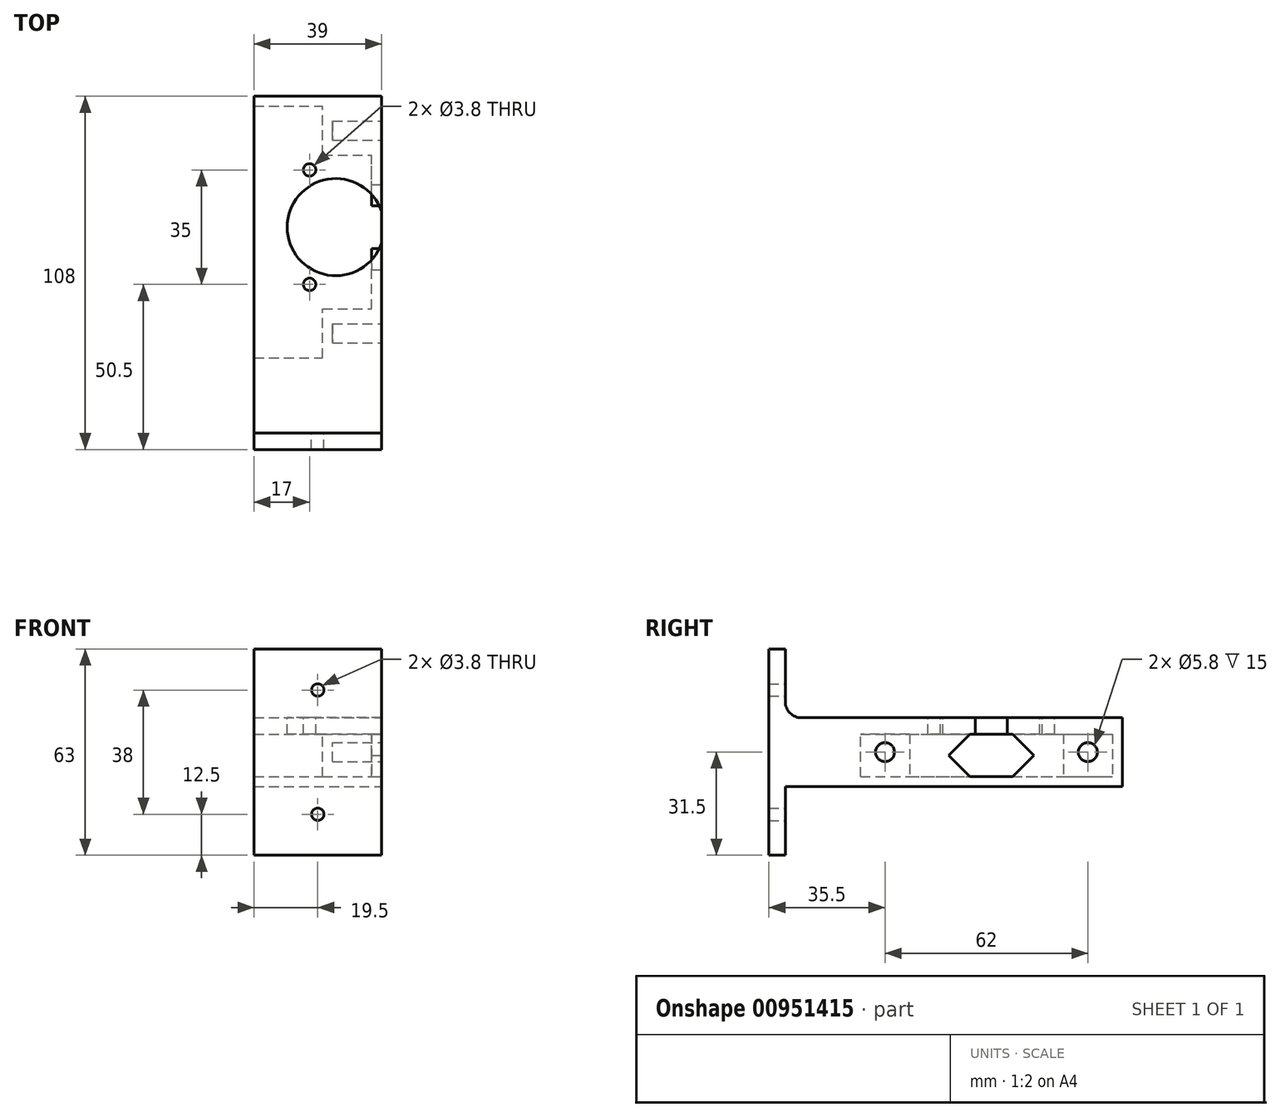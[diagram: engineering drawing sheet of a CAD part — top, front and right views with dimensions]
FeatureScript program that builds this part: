
annotation { "Feature Type Name" : "Feature", "Feature Type Description" : "" }
export const myFeature = defineFeature(function(context is Context, id is Id, definition is map)
    precondition{}
    {
        {
            var Q0;
            Q0=qCreatedBy(makeId("Top.planeOp"),FACE);
            var sketch = newSketch(context, id + "F0", { "sketchPlane" : qUnion([Q0])});
            skLineSegment(sketch, "E0", {"start": v(0, 83) * mm, "end": v(0, 0) * mm});
            skLineSegment(sketch, "E1", {"start": v(0, 0) * mm, "end": v(-39, 0) * mm});
            skLineSegment(sketch, "E2", {"start": v(-39, 0) * mm, "end": v(-39, 3) * mm});
            skLineSegment(sketch, "E3", {"start": v(-39, 3) * mm, "end": v(-3, 3) * mm});
            skLineSegment(sketch, "E4", {"start": v(-3, 3) * mm, "end": v(-3, 83) * mm});
            skLineSegment(sketch, "E5", {"start": v(-3, 83) * mm, "end": v(0, 83) * mm});
            skSolve(sketch);
        }
        {
            var Q0;
            Q0 = qSketchRegion(id + "F0", true);
            extrude(context, id + "F1", {"entities" : qUnion([Q0]), "endBound" : BoundingType.SYMMETRIC, "depth" : 18 * mm, "offsetDistance" : 25 * mm});
        }
        {
            var Q0;
            Q0=makeQuery(id+"F1.opExtrude","CAP_FACE",FACE,{"disambiguationData":[OSD([sQuery(id+"F0.wireOp",EDGE,"E0"),sQuery(id+"F0.wireOp",EDGE,"E1"),sQuery(id+"F0.wireOp",EDGE,"E2"),sQuery(id+"F0.wireOp",EDGE,"E3"),sQuery(id+"F0.wireOp",EDGE,"E4"),sQuery(id+"F0.wireOp",EDGE,"E5")])],"isStart":false});
            var sketch = newSketch(context, id + "F2", { "sketchPlane" : qUnion([Q0])});
            skLineSegment(sketch, "E6.0", {"start": v(0, 83) * mm, "end": v(0, 0) * mm});
            skLineSegment(sketch, "E6.1", {"start": v(0, 0) * mm, "end": v(-39, 0) * mm});
            skLineSegment(sketch, "E7", {"start": v(-39, 0) * mm, "end": v(-39, 83) * mm});
            skLineSegment(sketch, "E8", {"start": v(-39, 83) * mm, "end": v(0, 83) * mm});
            skSolve(sketch);
        }
        {
            var Q0;
            Q0 = qSketchRegion(id + "F2", true);
            extrude(context, id + "F3", {"entities" : qUnion([Q0]), "operationType" : NewBodyOperationType.ADD, "oppositeDirection" : true, "depth" : 5 * mm, "offsetDistance" : 25 * mm});
        }
        {
            var Q0;
            Q0=makeQuery(id+"F3.boolean.opBoolean","MERGE",FACE,{"derivedFrom":[makeQuery(id+"F1.opExtrude","CAP_FACE",FACE,{"disambiguationData":[OSD([sQuery(id+"F0.wireOp",EDGE,"E0"),sQuery(id+"F0.wireOp",EDGE,"E1"),sQuery(id+"F0.wireOp",EDGE,"E2"),sQuery(id+"F0.wireOp",EDGE,"E3"),sQuery(id+"F0.wireOp",EDGE,"E4"),sQuery(id+"F0.wireOp",EDGE,"E5")])],"isStart":false}),makeQuery(id+"F3.opExtrude","CAP_FACE",FACE,{"disambiguationData":[OSD([sQuery(id+"F2.wireOp",EDGE,"E6.0"),sQuery(id+"F2.wireOp",EDGE,"E6.1"),sQuery(id+"F2.wireOp",EDGE,"E7"),sQuery(id+"F2.wireOp",EDGE,"E8")])],"isStart":true})]});
            var sketch = newSketch(context, id + "F4", { "sketchPlane" : qUnion([Q0])});
            skCircle(sketch, "E9", {"center": v(-22, 60.5) * mm, "radius": 1.9 * mm});
            skCircle(sketch, "E10", {"center": v(-22, 25.5) * mm, "radius": 1.9 * mm});
            skLineSegment(sketch, "E11", {"start": v(-22, 60.5) * mm, "end": v(-22, 83) * mm});
            skLineSegment(sketch, "E12", {"start": v(-22, 25.5) * mm, "end": v(-22, 3) * mm});
            skSolve(sketch);
        }
        {
            var Q0;
            Q0=makeQuery(id+"F3.boolean.opBoolean","MERGE",FACE,{"derivedFrom":[makeQuery(id+"F1.opExtrude","SWEPT_FACE",FACE,{"disambiguationData":[OSD([sQuery(id+"F0.wireOp",EDGE,"E5")])]}),makeQuery(id+"F3.opExtrude","SWEPT_FACE",FACE,{"disambiguationData":[OSD([sQuery(id+"F2.wireOp",EDGE,"E8")])]})]});
            var sketch = newSketch(context, id + "F5", { "sketchPlane" : qUnion([Q0])});
            skLineSegment(sketch, "E13", {"start": v(0, 9) * mm, "end": v(18, 9) * mm});
            skLineSegment(sketch, "E14", {"start": v(18, 9) * mm, "end": v(18, -9) * mm});
            skLineSegment(sketch, "E15", {"start": v(18, -9) * mm, "end": v(0, -9) * mm});
            skLineSegment(sketch, "E16", {"start": v(0, -9) * mm, "end": v(0, 9) * mm});
            skSolve(sketch);
        }
        {
            var Q0;
            {var subQ5=makeQuery(id+"F1.opExtrude","SWEPT_EDGE",EDGE,{"disambiguationData":[OSD([sQuery(id+"F0.wireOp",EDGE,"E4"),sQuery(id+"F0.wireOp",EDGE,"E5")])]});Q0=makeQuery(id+"F5.imprint","IMPRINT",FACE,{"disambiguationData":[TD([[makeQuery(id+"F5.imprint","IMPRINT",EDGE,{"derivedFrom":subQ5}),1.0]])]});}
            extrude(context, id + "F6", {"entities" : qUnion([Q0]), "operationType" : NewBodyOperationType.ADD, "oppositeDirection" : true, "depth" : 18 * mm, "offsetDistance" : 25 * mm});
        }
        {
            var Q0;
            Q0=makeQuery(id+"F6.boolean.opBoolean","MERGE",FACE,{"derivedFrom":[makeQuery(id+"F1.opExtrude","CAP_FACE",FACE,{"disambiguationData":[OSD([sQuery(id+"F0.wireOp",EDGE,"E0"),sQuery(id+"F0.wireOp",EDGE,"E1"),sQuery(id+"F0.wireOp",EDGE,"E2"),sQuery(id+"F0.wireOp",EDGE,"E3"),sQuery(id+"F0.wireOp",EDGE,"E4"),sQuery(id+"F0.wireOp",EDGE,"E5")])],"isStart":true}),makeQuery(id+"F6.opExtrude","SWEPT_FACE",FACE,{"disambiguationData":[OSD([sQuery(id+"F5.wireOp",EDGE,"E15")])]})]});
            var sketch = newSketch(context, id + "F7", { "sketchPlane" : qUnion([Q0])});
            skLineSegment(sketch, "E17", {"start": v(0, 0) * mm, "end": v(-18, 0) * mm});
            skLineSegment(sketch, "E18", {"start": v(-18, 0) * mm, "end": v(-18, -18) * mm});
            skLineSegment(sketch, "E19", {"start": v(-18, -18) * mm, "end": v(0, -18) * mm});
            skLineSegment(sketch, "E20", {"start": v(0, -18) * mm, "end": v(0, 0) * mm});
            skSolve(sketch);
        }
        {
            var Q0;
            Q0 = qSketchRegion(id + "F7", true);
            extrude(context, id + "F8", {"entities" : qUnion([Q0]), "operationType" : NewBodyOperationType.ADD, "oppositeDirection" : true, "depth" : 18 * mm, "offsetDistance" : 25 * mm});
        }
        {
            var Q0;
            Q0=makeQuery(id+"F8.boolean.opBoolean","MERGE",FACE,{"derivedFrom":[makeQuery(id+"F6.boolean.opBoolean","MERGE",FACE,{"derivedFrom":[makeQuery(id+"F1.opExtrude","CAP_FACE",FACE,{"disambiguationData":[OSD([sQuery(id+"F0.wireOp",EDGE,"E0"),sQuery(id+"F0.wireOp",EDGE,"E1"),sQuery(id+"F0.wireOp",EDGE,"E2"),sQuery(id+"F0.wireOp",EDGE,"E3"),sQuery(id+"F0.wireOp",EDGE,"E4"),sQuery(id+"F0.wireOp",EDGE,"E5")])],"isStart":true}),makeQuery(id+"F6.opExtrude","SWEPT_FACE",FACE,{"disambiguationData":[OSD([sQuery(id+"F5.wireOp",EDGE,"E15")])]})]}),makeQuery(id+"F8.opExtrude","CAP_FACE",FACE,{"disambiguationData":[OSD([sQuery(id+"F7.wireOp",EDGE,"E17"),sQuery(id+"F7.wireOp",EDGE,"E18"),sQuery(id+"F7.wireOp",EDGE,"E19"),sQuery(id+"F7.wireOp",EDGE,"E20")])],"isStart":true})]});
            var sketch = newSketch(context, id + "F9", { "sketchPlane" : qUnion([Q0])});
            skLineSegment(sketch, "E21.0.0", {"start": v(0, -83) * mm, "end": v(-22, -83) * mm});
            skLineSegment(sketch, "E21.0.1", {"start": v(-22, -83) * mm, "end": v(-39, -83) * mm});
            skLineSegment(sketch, "E21.0.2", {"start": v(-39, -83) * mm, "end": v(-39, 0) * mm});
            skLineSegment(sketch, "E21.0.3", {"start": v(-39, 0) * mm, "end": v(0, 0) * mm});
            skLineSegment(sketch, "E21.0.4", {"start": v(0, 0) * mm, "end": v(0, -83) * mm});
            skSolve(sketch);
        }
        {
            var Q0;
            Q0 = qSketchRegion(id + "F9", true);
            extrude(context, id + "F10", {"entities" : qUnion([Q0]), "operationType" : NewBodyOperationType.ADD, "depth" : 3 * mm, "offsetDistance" : 25 * mm});
        }
        {
            var Q0;
            Q0=makeQuery(id+"F4.imprint","IMPRINT",FACE,{"disambiguationData":[TD([[makeQuery(id+"F4.imprint","IMPRINT",EDGE,{"derivedFrom":sQuery(id+"F4.wireOp",EDGE,"E9")}),-1.0]])]});
            var sketch = newSketch(context, id + "F11", { "sketchPlane" : qUnion([Q0])});
            skCircle(sketch, "E22", {"center": v(-14, 43) * mm, "radius": 17.34 * mm});
            skCircle(sketch, "E23", {"center": v(-14, 43) * mm, "radius": 14.84 * mm});
            skSolve(sketch);
        }
        {
            var Q0;
            {var subQ0=sQuery(id+"F11.wireOp",EDGE,"E23");var subQ1=makeQuery(id+"F4.imprint","IMPRINT",EDGE,{"derivedFrom":makeQuery(id+"F1.opExtrude","CAP_EDGE",EDGE,{"disambiguationData":[OSD([sQuery(id+"F0.wireOp",EDGE,"E0")])],"isStart":false})});var subQ2=makeQuery(id+"F11.imprint","INTERSECT",VERTEX,{"disambiguationData":[OD(0.0)],"derivedFrom":[subQ1,subQ0]});Q0=makeQuery(id+"F11.imprint","IMPRINT",FACE,{"disambiguationData":[TD([[makeQuery(id+"F11.imprint","IMPRINT",EDGE,{"disambiguationData":[TD([[subQ2,-1.0]])],"derivedFrom":subQ0}),1.0]])]});}
            var Q1;
            Q1=makeQuery(id+"F3.opExtrude","CAP_FACE",FACE,{"disambiguationData":[OSD([sQuery(id+"F2.wireOp",EDGE,"E6.0"),sQuery(id+"F2.wireOp",EDGE,"E6.1"),sQuery(id+"F2.wireOp",EDGE,"E7"),sQuery(id+"F2.wireOp",EDGE,"E8")])],"isStart":false});
            extrude(context, id + "F12", {"entities" : qUnion([Q0]), "operationType" : NewBodyOperationType.REMOVE, "endBound" : BoundingType.UP_TO_SURFACE, "oppositeDirection" : true, "depth" : 25 * mm, "endBoundEntityFace" : qUnion([Q1]), "offsetDistance" : 25 * mm});
        }
        {
            var Q0;
            Q0=makeQuery(id+"F10.boolean.opBoolean","MERGE",FACE,{"derivedFrom":[makeQuery(id+"F1.opExtrude","SWEPT_FACE",FACE,{"disambiguationData":[OSD([sQuery(id+"F0.wireOp",EDGE,"E0")])]}),makeQuery(id+"F10.opExtrude","SWEPT_FACE",FACE,{"disambiguationData":[OSD([sQuery(id+"F9.wireOp",EDGE,"E21.0.4")])]})]});
            var sketch = newSketch(context, id + "F13", { "sketchPlane" : qUnion([Q0])});
            skLineSegment(sketch, "E24.top", {"start": v(36.5, -9) * mm, "end": v(49.5, -9) * mm});
            skLineSegment(sketch, "E24.left", {"start": v(36.5, 4) * mm, "end": v(36.5, -9) * mm});
            skLineSegment(sketch, "E24.right", {"start": v(49.5, 4) * mm, "end": v(49.5, -9) * mm});
            skLineSegment(sketch, "E25", {"start": v(36.5, 4) * mm, "end": v(30, -2.5) * mm});
            skPoint(sketch, "E25.endSnap0", {"position": v(36.5, -2.5) * mm});
            skLineSegment(sketch, "E26", {"start": v(30, -2.5) * mm, "end": v(36.5, -9) * mm});
            skLineSegment(sketch, "E27", {"start": v(49.5, 4) * mm, "end": v(56, -2.5) * mm});
            skLineSegment(sketch, "E28", {"start": v(56, -2.5) * mm, "end": v(49.5, -9) * mm});
            skLineSegment(sketch, "E29", {"start": v(36.5, 4) * mm, "end": v(38.07, 4) * mm});
            skLineSegment(sketch, "E30", {"start": v(47.93, 4) * mm, "end": v(49.5, 4) * mm});
            skLineSegment(sketch, "E31", {"start": v(38.07, 4) * mm, "end": v(47.93, 4) * mm});
            skCircle(sketch, "E32", {"center": v(10.5, -1.5) * mm, "radius": 2.9 * mm});
            skCircle(sketch, "E33", {"center": v(72.5, -1.5) * mm, "radius": 2.9 * mm});
            skLineSegment(sketch, "E34", {"start": v(0, -1.5) * mm, "end": v(10.5, -1.5) * mm});
            skLineSegment(sketch, "E35", {"start": v(72.5, -1.5) * mm, "end": v(83, -1.5) * mm});
            skLineSegment(sketch, "E36", {"start": v(10.5, -1.5) * mm, "end": v(10.5, -12) * mm});
            skSolve(sketch);
        }
        {
            var Q0;
            {var subQ0=sQuery(id+"F13.wireOp",EDGE,"E34");var subQ1=sQuery(id+"F13.wireOp",EDGE,"E32");var subQ2=makeQuery(id+"F13.imprint","INTERSECT",VERTEX,{"derivedFrom":[subQ1,subQ0]});Q0=makeQuery(id+"F13.imprint","IMPRINT",FACE,{"disambiguationData":[TD([[makeQuery(id+"F13.imprint","IMPRINT",EDGE,{"disambiguationData":[TD([[subQ2,-1.0]])],"derivedFrom":subQ1}),1.0]])]});}
            var Q1;
            {var subQ0=sQuery(id+"F13.wireOp",EDGE,"E34");var subQ1=sQuery(id+"F13.wireOp",EDGE,"E32");var subQ2=makeQuery(id+"F13.imprint","INTERSECT",VERTEX,{"derivedFrom":[subQ1,subQ0]});Q1=makeQuery(id+"F13.imprint","IMPRINT",FACE,{"disambiguationData":[TD([[makeQuery(id+"F13.imprint","IMPRINT",EDGE,{"disambiguationData":[TD([[subQ2,1.0]])],"derivedFrom":subQ1}),1.0]])]});}
            var Q2;
            Q2=makeQuery(id+"F13.imprint","IMPRINT",FACE,{"disambiguationData":[TD([[makeQuery(id+"F13.imprint","IMPRINT",EDGE,{"derivedFrom":sQuery(id+"F13.wireOp",EDGE,"E24.left")}),-1.0]])]});
            var Q3;
            Q3=makeQuery(id+"F13.imprint","IMPRINT",FACE,{"disambiguationData":[TD([[makeQuery(id+"F13.imprint","IMPRINT",EDGE,{"derivedFrom":sQuery(id+"F13.wireOp",EDGE,"E24.top")}),1.0]])]});
            var Q4;
            Q4=makeQuery(id+"F13.imprint","IMPRINT",FACE,{"disambiguationData":[TD([[makeQuery(id+"F13.imprint","IMPRINT",EDGE,{"derivedFrom":sQuery(id+"F13.wireOp",EDGE,"E24.right")}),1.0]])]});
            var Q5;
            Q5=makeQuery(id+"F13.imprint","IMPRINT",FACE,{"disambiguationData":[TD([[makeQuery(id+"F13.imprint","IMPRINT",EDGE,{"derivedFrom":sQuery(id+"F13.wireOp",EDGE,"E33")}),1.0]])]});
            extrude(context, id + "F14", {"entities" : qUnion([Q0, Q1, Q2, Q3, Q4, Q5]), "operationType" : NewBodyOperationType.REMOVE, "oppositeDirection" : true, "depth" : 15 * mm, "offsetDistance" : 25 * mm});
        }
        {
            var Q0;
            Q0=makeQuery(id+"F6.opExtrude","SWEPT_FACE",FACE,{"disambiguationData":[OSD([sQuery(id+"F5.wireOp",EDGE,"E14")])]});
            var sketch = newSketch(context, id + "F15", { "sketchPlane" : qUnion([Q0])});
            skLineSegment(sketch, "E37", {"start": v(-83, 4) * mm, "end": v(-80, 4) * mm});
            skLineSegment(sketch, "E38", {"start": v(-80, 4) * mm, "end": v(-80, -9) * mm});
            skLineSegment(sketch, "E39", {"start": v(-80, -9) * mm, "end": v(-83, -9) * mm});
            skLineSegment(sketch, "E40", {"start": v(-83, -9) * mm, "end": v(-83, 4) * mm});
            skSolve(sketch);
        }
        {
            var Q0;
            Q0=makeQuery(id+"F15.imprint","IMPRINT",FACE,{"disambiguationData":[TD([[makeQuery(id+"F15.imprint","IMPRINT",EDGE,{"derivedFrom":sQuery(id+"F15.wireOp",EDGE,"E37")}),1.0]])]});
            var Q1;
            Q1=makeQuery(id+"F10.boolean.opBoolean","MERGE",FACE,{"derivedFrom":[makeQuery(id+"F3.boolean.opBoolean","MERGE",FACE,{"derivedFrom":[makeQuery(id+"F1.opExtrude","SWEPT_FACE",FACE,{"disambiguationData":[OSD([sQuery(id+"F0.wireOp",EDGE,"E2")])]}),makeQuery(id+"F3.opExtrude","SWEPT_FACE",FACE,{"disambiguationData":[OSD([sQuery(id+"F2.wireOp",EDGE,"E7")])]})]}),makeQuery(id+"F10.opExtrude","SWEPT_FACE",FACE,{"disambiguationData":[OSD([sQuery(id+"F9.wireOp",EDGE,"E21.0.2")])]})]});
            extrude(context, id + "F16", {"entities" : qUnion([Q0]), "operationType" : NewBodyOperationType.ADD, "endBound" : BoundingType.UP_TO_SURFACE, "depth" : 25 * mm, "endBoundEntityFace" : qUnion([Q1]), "offsetDistance" : 25 * mm});
        }
        {
            var Q0;
            Q0=makeQuery(id+"F4.imprint","IMPRINT",FACE,{"disambiguationData":[TD([[makeQuery(id+"F4.imprint","IMPRINT",EDGE,{"derivedFrom":sQuery(id+"F4.wireOp",EDGE,"E9")}),1.0]])]});
            var Q1;
            Q1=makeQuery(id+"F4.imprint","IMPRINT",FACE,{"disambiguationData":[TD([[makeQuery(id+"F4.imprint","IMPRINT",EDGE,{"derivedFrom":sQuery(id+"F4.wireOp",EDGE,"E10")}),1.0]])]});
            var Q2;
            Q2=makeQuery(id+"F3.opExtrude","CAP_FACE",FACE,{"disambiguationData":[OSD([sQuery(id+"F2.wireOp",EDGE,"E6.0"),sQuery(id+"F2.wireOp",EDGE,"E6.1"),sQuery(id+"F2.wireOp",EDGE,"E7"),sQuery(id+"F2.wireOp",EDGE,"E8")])],"isStart":false});
            extrude(context, id + "F17", {"entities" : qUnion([Q0, Q1]), "operationType" : NewBodyOperationType.REMOVE, "endBound" : BoundingType.UP_TO_SURFACE, "oppositeDirection" : true, "depth" : 25 * mm, "endBoundEntityFace" : qUnion([Q2]), "offsetDistance" : 25 * mm});
        }
        {
            var Q0;
            Q0=makeQuery(id+"F10.boolean.opBoolean","MERGE",FACE,{"derivedFrom":[makeQuery(id+"F1.opExtrude","SWEPT_FACE",FACE,{"disambiguationData":[OSD([sQuery(id+"F0.wireOp",EDGE,"E1")])]}),makeQuery(id+"F10.opExtrude","SWEPT_FACE",FACE,{"disambiguationData":[OSD([sQuery(id+"F9.wireOp",EDGE,"E21.0.3")])]})]});
            var sketch = newSketch(context, id + "F18", { "sketchPlane" : qUnion([Q0])});
            skLineSegment(sketch, "E41.0", {"start": v(0, -12) * mm, "end": v(-39, -12) * mm});
            skLineSegment(sketch, "E41.1", {"start": v(0, 9) * mm, "end": v(0, -12) * mm});
            skLineSegment(sketch, "E41.2", {"start": v(0, 9) * mm, "end": v(-39, 9) * mm});
            skLineSegment(sketch, "E41.3", {"start": v(-39, 9) * mm, "end": v(-39, -12) * mm});
            skSolve(sketch);
        }
        {
            var Q0;
            Q0=makeQuery(id+"F18.imprint","IMPRINT",FACE,{"disambiguationData":[TD([[makeQuery(id+"F18.imprint","IMPRINT",EDGE,{"derivedFrom":sQuery(id+"F18.wireOp",EDGE,"E41.0")}),-1.0]])]});
            extrude(context, id + "F19", {"entities" : qUnion([Q0]), "operationType" : NewBodyOperationType.ADD, "depth" : 20 * mm, "offsetDistance" : 25 * mm});
        }
        {
            var Q0;
            Q0=makeQuery(id+"F19.opExtrude","CAP_FACE",FACE,{"disambiguationData":[OSD([sQuery(id+"F18.wireOp",EDGE,"E41.0"),sQuery(id+"F18.wireOp",EDGE,"E41.1"),sQuery(id+"F18.wireOp",EDGE,"E41.2"),sQuery(id+"F18.wireOp",EDGE,"E41.3")])],"isStart":false});
            var sketch = newSketch(context, id + "F20", { "sketchPlane" : qUnion([Q0])});
            skLineSegment(sketch, "E42", {"start": v(-39, 30) * mm, "end": v(-39, 9) * mm});
            skLineSegment(sketch, "E43", {"start": v(-39, 9) * mm, "end": v(-39, -12) * mm});
            skLineSegment(sketch, "E44", {"start": v(-39, -12) * mm, "end": v(-39, -33) * mm});
            skLineSegment(sketch, "E45", {"start": v(-39, -33) * mm, "end": v(0, -33) * mm});
            skLineSegment(sketch, "E46", {"start": v(0, -33) * mm, "end": v(0, -12) * mm});
            skLineSegment(sketch, "E47", {"start": v(0, -12) * mm, "end": v(0, 9) * mm});
            skLineSegment(sketch, "E48", {"start": v(0, 9) * mm, "end": v(0, 30) * mm});
            skLineSegment(sketch, "E49", {"start": v(0, 30) * mm, "end": v(-39, 30) * mm});
            skSolve(sketch);
        }
        {
            var Q0;
            Q0 = qSketchRegion(id + "F20", true);
            extrude(context, id + "F21", {"entities" : qUnion([Q0]), "operationType" : NewBodyOperationType.ADD, "depth" : 3 * mm, "offsetDistance" : 25 * mm});
        }
        {
            var Q0;
            Q0=makeQuery(id+"F19.opExtrude","CAP_EDGE",EDGE,{"disambiguationData":[OSD([sQuery(id+"F18.wireOp",EDGE,"E41.0")])],"isStart":false});
            var Q1;
            Q1=makeQuery(id+"F19.opExtrude","CAP_EDGE",EDGE,{"disambiguationData":[OSD([sQuery(id+"F18.wireOp",EDGE,"E41.2")])],"isStart":false});
            fillet(context, id + "F22", {"entities" : qUnion([Q0, Q1]), "radius" : 5 * mm, "tangentPropagation" : true, "allowEdgeOverflow" : false});
        }
        {
            var Q0;
            Q0=makeQuery(id+"F21.opExtrude","CAP_FACE",FACE,{"disambiguationData":[OSD([sQuery(id+"F20.wireOp",EDGE,"E42"),sQuery(id+"F20.wireOp",EDGE,"E43"),sQuery(id+"F20.wireOp",EDGE,"E44"),sQuery(id+"F20.wireOp",EDGE,"E45"),sQuery(id+"F20.wireOp",EDGE,"E46"),sQuery(id+"F20.wireOp",EDGE,"E47"),sQuery(id+"F20.wireOp",EDGE,"E48"),sQuery(id+"F20.wireOp",EDGE,"E49")])],"isStart":false});
            var sketch = newSketch(context, id + "F23", { "sketchPlane" : qUnion([Q0])});
            skLineSegment(sketch, "E50.bottom", {"start": v(-32, 23) * mm, "end": v(-7, 23) * mm});
            skLineSegment(sketch, "E50.top", {"start": v(-32, -26) * mm, "end": v(-7, -26) * mm});
            skLineSegment(sketch, "E50.left", {"start": v(-32, 23) * mm, "end": v(-32, -26) * mm});
            skLineSegment(sketch, "E50.right", {"start": v(-7, 23) * mm, "end": v(-7, -26) * mm});
            skCircle(sketch, "E51", {"center": v(-32, -26) * mm, "radius": 1.9 * mm});
            skCircle(sketch, "E52", {"center": v(-7, -26) * mm, "radius": 1.9 * mm});
            skCircle(sketch, "E53", {"center": v(-7, 23) * mm, "radius": 1.9 * mm});
            skCircle(sketch, "E54", {"center": v(-32, 23) * mm, "radius": 1.9 * mm});
            skSolve(sketch);
        }
        {
            var Q0;
            {var subQ0=sQuery(id+"F23.wireOp",EDGE,"E50.left");var subQ1=sQuery(id+"F23.wireOp",EDGE,"E50.bottom");var subQ2=makeQuery(id+"F23.imprint","INTERSECT",VERTEX,{"derivedFrom":[subQ1,subQ0]});Q0=makeQuery(id+"F23.imprint","IMPRINT",FACE,{"disambiguationData":[TD([[makeQuery(id+"F23.imprint","IMPRINT",EDGE,{"disambiguationData":[TD([[subQ2,-1.0]])],"derivedFrom":subQ1}),1.0]])]});}
            var Q1;
            {var subQ0=sQuery(id+"F23.wireOp",EDGE,"E50.left");var subQ1=sQuery(id+"F23.wireOp",EDGE,"E50.bottom");var subQ2=makeQuery(id+"F23.imprint","INTERSECT",VERTEX,{"derivedFrom":[subQ1,subQ0]});Q1=makeQuery(id+"F23.imprint","IMPRINT",FACE,{"disambiguationData":[TD([[makeQuery(id+"F23.imprint","IMPRINT",EDGE,{"disambiguationData":[TD([[subQ2,-1.0]])],"derivedFrom":subQ1}),-1.0]])]});}
            var Q2;
            {var subQ0=sQuery(id+"F23.wireOp",EDGE,"E50.right");var subQ1=sQuery(id+"F23.wireOp",EDGE,"E50.bottom");var subQ2=makeQuery(id+"F23.imprint","INTERSECT",VERTEX,{"derivedFrom":[subQ1,subQ0]});Q2=makeQuery(id+"F23.imprint","IMPRINT",FACE,{"disambiguationData":[TD([[makeQuery(id+"F23.imprint","IMPRINT",EDGE,{"disambiguationData":[TD([[subQ2,1.0]])],"derivedFrom":subQ1}),1.0]])]});}
            var Q3;
            {var subQ0=sQuery(id+"F23.wireOp",EDGE,"E50.right");var subQ1=sQuery(id+"F23.wireOp",EDGE,"E50.bottom");var subQ2=makeQuery(id+"F23.imprint","INTERSECT",VERTEX,{"derivedFrom":[subQ1,subQ0]});Q3=makeQuery(id+"F23.imprint","IMPRINT",FACE,{"disambiguationData":[TD([[makeQuery(id+"F23.imprint","IMPRINT",EDGE,{"disambiguationData":[TD([[subQ2,1.0]])],"derivedFrom":subQ1}),-1.0]])]});}
            var Q4;
            {var subQ0=sQuery(id+"F23.wireOp",EDGE,"E50.left");var subQ1=sQuery(id+"F23.wireOp",EDGE,"E50.top");var subQ2=makeQuery(id+"F23.imprint","INTERSECT",VERTEX,{"derivedFrom":[subQ1,subQ0]});Q4=makeQuery(id+"F23.imprint","IMPRINT",FACE,{"disambiguationData":[TD([[makeQuery(id+"F23.imprint","IMPRINT",EDGE,{"disambiguationData":[TD([[subQ2,-1.0]])],"derivedFrom":subQ1}),-1.0]])]});}
            var Q5;
            {var subQ0=sQuery(id+"F23.wireOp",EDGE,"E50.left");var subQ1=sQuery(id+"F23.wireOp",EDGE,"E50.top");var subQ2=makeQuery(id+"F23.imprint","INTERSECT",VERTEX,{"derivedFrom":[subQ1,subQ0]});Q5=makeQuery(id+"F23.imprint","IMPRINT",FACE,{"disambiguationData":[TD([[makeQuery(id+"F23.imprint","IMPRINT",EDGE,{"disambiguationData":[TD([[subQ2,-1.0]])],"derivedFrom":subQ1}),1.0]])]});}
            var Q6;
            {var subQ0=sQuery(id+"F23.wireOp",EDGE,"E50.right");var subQ1=sQuery(id+"F23.wireOp",EDGE,"E50.top");var subQ2=makeQuery(id+"F23.imprint","INTERSECT",VERTEX,{"derivedFrom":[subQ1,subQ0]});Q6=makeQuery(id+"F23.imprint","IMPRINT",FACE,{"disambiguationData":[TD([[makeQuery(id+"F23.imprint","IMPRINT",EDGE,{"disambiguationData":[TD([[subQ2,1.0]])],"derivedFrom":subQ1}),-1.0]])]});}
            var Q7;
            {var subQ0=sQuery(id+"F23.wireOp",EDGE,"E50.right");var subQ1=sQuery(id+"F23.wireOp",EDGE,"E50.top");var subQ2=makeQuery(id+"F23.imprint","INTERSECT",VERTEX,{"derivedFrom":[subQ1,subQ0]});Q7=makeQuery(id+"F23.imprint","IMPRINT",FACE,{"disambiguationData":[TD([[makeQuery(id+"F23.imprint","IMPRINT",EDGE,{"disambiguationData":[TD([[subQ2,1.0]])],"derivedFrom":subQ1}),1.0]])]});}
            extrude(context, id + "F24", {"entities" : qUnion([Q0, Q1, Q2, Q3, Q4, Q5, Q6, Q7]), "operationType" : NewBodyOperationType.REMOVE, "oppositeDirection" : true, "depth" : 25 * mm, "offsetDistance" : 25 * mm});
        }
        {
            var Q0;
            Q0=makeQuery(id+"F21.boolean.opBoolean","MERGE",FACE,{"derivedFrom":[makeQuery(id+"F19.boolean.opBoolean","MERGE",FACE,{"derivedFrom":[makeQuery(id+"F10.boolean.opBoolean","MERGE",FACE,{"derivedFrom":[makeQuery(id+"F1.opExtrude","SWEPT_FACE",FACE,{"disambiguationData":[OSD([sQuery(id+"F0.wireOp",EDGE,"E0")])]}),makeQuery(id+"F10.opExtrude","SWEPT_FACE",FACE,{"disambiguationData":[OSD([sQuery(id+"F9.wireOp",EDGE,"E21.0.4")])]})]}),makeQuery(id+"F19.opExtrude","SWEPT_FACE",FACE,{"disambiguationData":[OSD([sQuery(id+"F18.wireOp",EDGE,"E41.1")])]})]}),makeQuery(id+"F21.opExtrude","SWEPT_FACE",FACE,{"disambiguationData":[OSD([sQuery(id+"F20.wireOp",EDGE,"E46"),sQuery(id+"F20.wireOp",EDGE,"E47"),sQuery(id+"F20.wireOp",EDGE,"E48")])]})]});
            var sketch = newSketch(context, id + "F25", { "sketchPlane" : qUnion([Q0])});
            skLineSegment(sketch, "E55", {"start": v(10.5, -1.5) * mm, "end": v(72.5, -1.5) * mm});
            skSolve(sketch);
        }
        {
            var Q0;
            {var subQ0=sQuery(id+"F20.wireOp",EDGE,"E48");var subQ1=sQuery(id+"F20.wireOp",EDGE,"E47");var subQ2=sQuery(id+"F20.wireOp",EDGE,"E46");var subQ6=sQuery(id+"F20.wireOp",EDGE,"E44");var subQ7=sQuery(id+"F20.wireOp",EDGE,"E43");var subQ8=sQuery(id+"F20.wireOp",EDGE,"E42");var subQ9=sQuery(id+"F20.wireOp",EDGE,"E49");Q0=makeQuery(id+"F21.boolean.opBoolean","SPLIT",FACE,{"disambiguationData":[TD([makeQuery(id+"F19.opExtrude","SWEPT_FACE",FACE,{"disambiguationData":[OSD([sQuery(id+"F18.wireOp",EDGE,"E41.2")])]})])],"derivedFrom":makeQuery(id+"F21.opExtrude","CAP_FACE",FACE,{"disambiguationData":[OSD([subQ8,subQ7,subQ6,sQuery(id+"F20.wireOp",EDGE,"E45"),subQ2,subQ1,subQ0,subQ9])],"isStart":true})});}
            var sketch = newSketch(context, id + "F26", { "sketchPlane" : qUnion([Q0])});
            skCircle(sketch, "E56", {"center": v(32, 23) * mm, "radius": 3.7 * mm});
            skCircle(sketch, "E57", {"center": v(7, 23) * mm, "radius": 2.7 * mm});
            skCircle(sketch, "E58", {"center": v(31.52, -25.8) * mm, "radius": 3.25 * mm});
            skCircle(sketch, "E59", {"center": v(7.08, -26.27) * mm, "radius": 2.44 * mm});
            skSolve(sketch);
        }
        {
            var Q0;
            Q0 = qSketchRegion(id + "F26", true);
            var Q1;
            Q1=makeQuery(id+"F21.opExtrude","CAP_FACE",FACE,{"disambiguationData":[OSD([sQuery(id+"F20.wireOp",EDGE,"E42"),sQuery(id+"F20.wireOp",EDGE,"E43"),sQuery(id+"F20.wireOp",EDGE,"E44"),sQuery(id+"F20.wireOp",EDGE,"E45"),sQuery(id+"F20.wireOp",EDGE,"E46"),sQuery(id+"F20.wireOp",EDGE,"E47"),sQuery(id+"F20.wireOp",EDGE,"E48"),sQuery(id+"F20.wireOp",EDGE,"E49")])],"isStart":false});
            extrude(context, id + "F27", {"entities" : qUnion([Q0]), "operationType" : NewBodyOperationType.ADD, "endBound" : BoundingType.UP_TO_SURFACE, "oppositeDirection" : true, "depth" : 25 * mm, "endBoundEntityFace" : qUnion([Q1]), "offsetDistance" : 25 * mm});
        }
        {
            var Q0;
            {var subQ0=sQuery(id+"F20.wireOp",EDGE,"E48");var subQ1=sQuery(id+"F20.wireOp",EDGE,"E47");var subQ2=sQuery(id+"F20.wireOp",EDGE,"E46");var subQ6=sQuery(id+"F20.wireOp",EDGE,"E44");var subQ7=sQuery(id+"F20.wireOp",EDGE,"E43");var subQ8=sQuery(id+"F20.wireOp",EDGE,"E42");var subQ9=sQuery(id+"F20.wireOp",EDGE,"E49");Q0=makeQuery(id+"F27.boolean.opBoolean","MERGE",FACE,{"derivedFrom":[makeQuery(id+"F21.boolean.opBoolean","SPLIT",FACE,{"disambiguationData":[TD([makeQuery(id+"F19.opExtrude","SWEPT_FACE",FACE,{"disambiguationData":[OSD([sQuery(id+"F18.wireOp",EDGE,"E41.2")])]})])],"derivedFrom":makeQuery(id+"F21.opExtrude","CAP_FACE",FACE,{"disambiguationData":[OSD([subQ8,subQ7,subQ6,sQuery(id+"F20.wireOp",EDGE,"E45"),subQ2,subQ1,subQ0,subQ9])],"isStart":true})}),makeQuery(id+"F27.opExtrude","CAP_FACE",FACE,{"disambiguationData":[OSD([sQuery(id+"F26.wireOp",EDGE,"E56")])],"isStart":true}),makeQuery(id+"F27.opExtrude","CAP_FACE",FACE,{"disambiguationData":[OSD([sQuery(id+"F26.wireOp",EDGE,"E57")])],"isStart":true})]});}
            var sketch = newSketch(context, id + "F28", { "sketchPlane" : qUnion([Q0])});
            skCircle(sketch, "E60", {"center": v(19.5, 17.5) * mm, "radius": 1.9 * mm});
            skCircle(sketch, "E61", {"center": v(19.5, -20.5) * mm, "radius": 1.9 * mm});
            skLineSegment(sketch, "E62", {"start": v(19.5, 17.5) * mm, "end": v(19.5, -20.5) * mm});
            skLineSegment(sketch, "E63", {"start": v(19.5, 17.5) * mm, "end": v(19.5, 30) * mm});
            skLineSegment(sketch, "E64", {"start": v(19.5, -20.5) * mm, "end": v(19.5, -33) * mm});
            skSolve(sketch);
        }
        {
            var Q0;
            Q0 = qSketchRegion(id + "F28", true);
            extrude(context, id + "F29", {"entities" : qUnion([Q0]), "operationType" : NewBodyOperationType.REMOVE, "oppositeDirection" : true, "depth" : 25 * mm, "offsetDistance" : 25 * mm});
        }
        {
            var Q0;
            Q0=makeQuery(id+"F27.boolean.opBoolean","MERGE",FACE,{"derivedFrom":[makeQuery(id+"F21.opExtrude","CAP_FACE",FACE,{"disambiguationData":[OSD([sQuery(id+"F20.wireOp",EDGE,"E42"),sQuery(id+"F20.wireOp",EDGE,"E43"),sQuery(id+"F20.wireOp",EDGE,"E44"),sQuery(id+"F20.wireOp",EDGE,"E45"),sQuery(id+"F20.wireOp",EDGE,"E46"),sQuery(id+"F20.wireOp",EDGE,"E47"),sQuery(id+"F20.wireOp",EDGE,"E48"),sQuery(id+"F20.wireOp",EDGE,"E49")])],"isStart":false}),makeQuery(id+"F27.opExtrude","CAP_FACE",FACE,{"disambiguationData":[OSD([sQuery(id+"F26.wireOp",EDGE,"E56")])],"isStart":false}),makeQuery(id+"F27.opExtrude","CAP_FACE",FACE,{"disambiguationData":[OSD([sQuery(id+"F26.wireOp",EDGE,"E57")])],"isStart":false}),makeQuery(id+"F27.opExtrude","CAP_FACE",FACE,{"disambiguationData":[OSD([sQuery(id+"F26.wireOp",EDGE,"E58")])],"isStart":false}),makeQuery(id+"F27.opExtrude","CAP_FACE",FACE,{"disambiguationData":[OSD([sQuery(id+"F26.wireOp",EDGE,"E59")])],"isStart":false})]});
            extrude(context, id + "F30", {"entities" : qUnion([Q0]), "operationType" : NewBodyOperationType.ADD, "depth" : 2 * mm, "offsetDistance" : 25 * mm});
        }
    });
